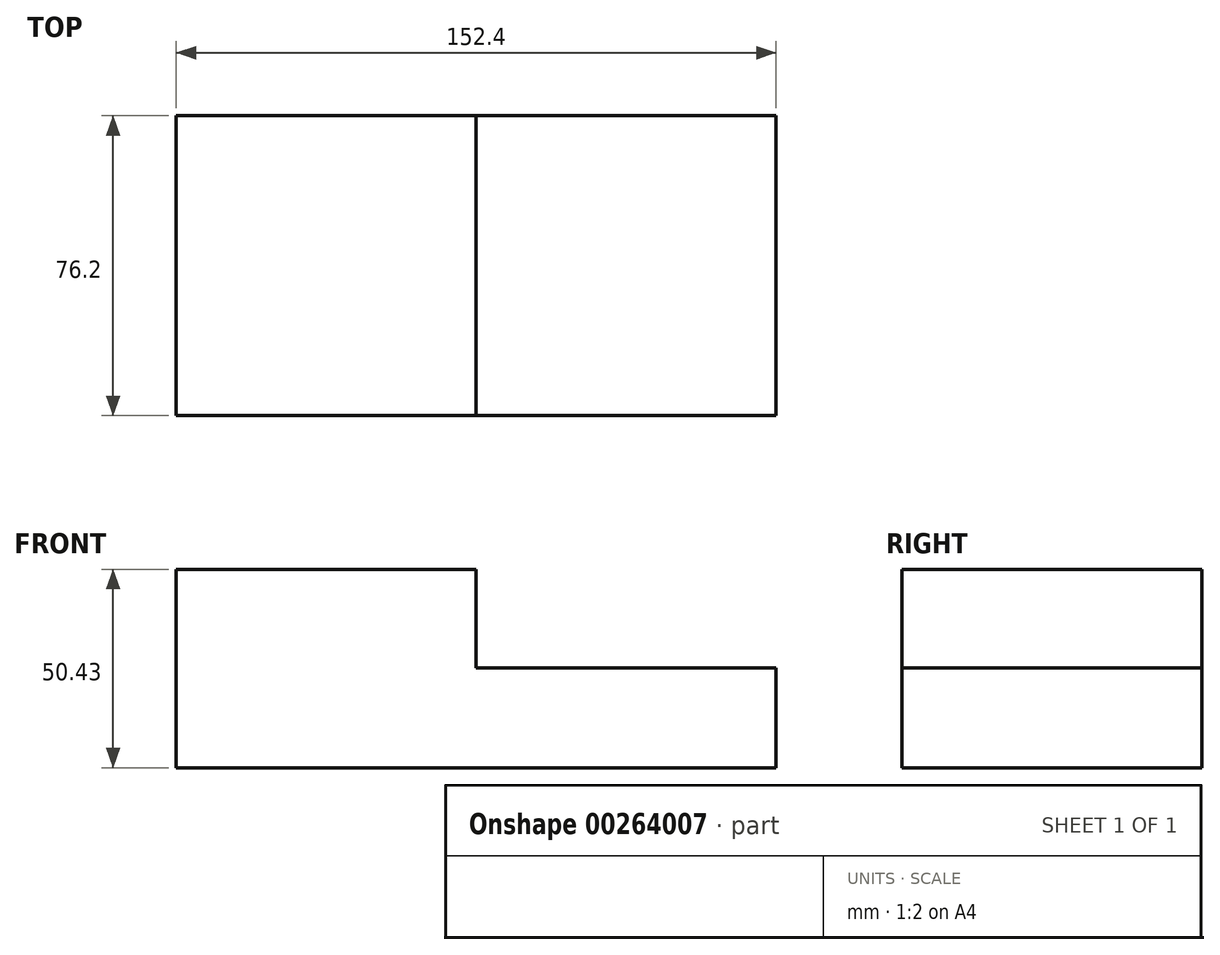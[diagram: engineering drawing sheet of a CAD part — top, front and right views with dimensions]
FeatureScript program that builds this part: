
annotation { "Feature Type Name" : "Feature", "Feature Type Description" : "" }
export const myFeature = defineFeature(function(context is Context, id is Id, definition is map)
    precondition{}
    {
        {
            var Q0;
            Q0=qCreatedBy(makeId("Front.planeOp"),FACE);
            var sketch = newSketch(context, id + "F0", { "sketchPlane" : qUnion([Q0])});
            skLineSegment(sketch, "E0.bottom", {"start": v(-76.2, 0) * mm, "end": v(76.2, 0) * mm});
            skLineSegment(sketch, "E0.top", {"start": v(-76.2, 25.4) * mm, "end": v(76.2, 25.4) * mm});
            skLineSegment(sketch, "E0.left", {"start": v(-76.2, 0) * mm, "end": v(-76.2, 25.4) * mm});
            skLineSegment(sketch, "E0.right", {"start": v(76.2, 0) * mm, "end": v(76.2, 25.4) * mm});
            skLineSegment(sketch, "E1.bottom", {"start": v(-76.2, 25.4) * mm, "end": v(0, 25.4) * mm});
            skLineSegment(sketch, "E1.top", {"start": v(-76.2, 50.8) * mm, "end": v(0, 50.8) * mm});
            skLineSegment(sketch, "E1.left", {"start": v(-76.2, 25.4) * mm, "end": v(-76.2, 50.8) * mm});
            skLineSegment(sketch, "E1.right", {"start": v(0, 25.4) * mm, "end": v(0, 50.8) * mm});
            skSolve(sketch);
        }
        {
            var Q0;
            Q0=makeQuery(id+"F0.imprint","IMPRINT",FACE,{"disambiguationData":[TD([[makeQuery(id+"F0.imprint","IMPRINT",EDGE,{"derivedFrom":sQuery(id+"F0.wireOp",EDGE,"E0.bottom")}),1.0]])]});
            extrude(context, id + "F1", {"entities" : qUnion([Q0]), "depth" : 76.2 * mm});
        }
        {
            var Q0;
            Q0=qCreatedBy(makeId("Front.planeOp"),FACE);
            var sketch = newSketch(context, id + "F2", { "sketchPlane" : qUnion([Q0])});
            skLineSegment(sketch, "E2.bottom", {"start": v(-76.2, 25.03) * mm, "end": v(0, 25.03) * mm});
            skLineSegment(sketch, "E2.top", {"start": v(-76.2, 50.43) * mm, "end": v(0, 50.43) * mm});
            skLineSegment(sketch, "E2.left", {"start": v(-76.2, 25.03) * mm, "end": v(-76.2, 50.43) * mm});
            skLineSegment(sketch, "E2.right", {"start": v(0, 25.03) * mm, "end": v(0, 50.43) * mm});
            skSolve(sketch);
        }
        {
            var Q0;
            Q0=makeQuery(id+"F2.imprint","IMPRINT",FACE,{"disambiguationData":[TD([[makeQuery(id+"F2.imprint","IMPRINT",EDGE,{"derivedFrom":sQuery(id+"F2.wireOp",EDGE,"E2.bottom")}),1.0]])]});
            extrude(context, id + "F3", {"entities" : qUnion([Q0]), "operationType" : NewBodyOperationType.ADD, "depth" : 76.2 * mm});
        }
    });
